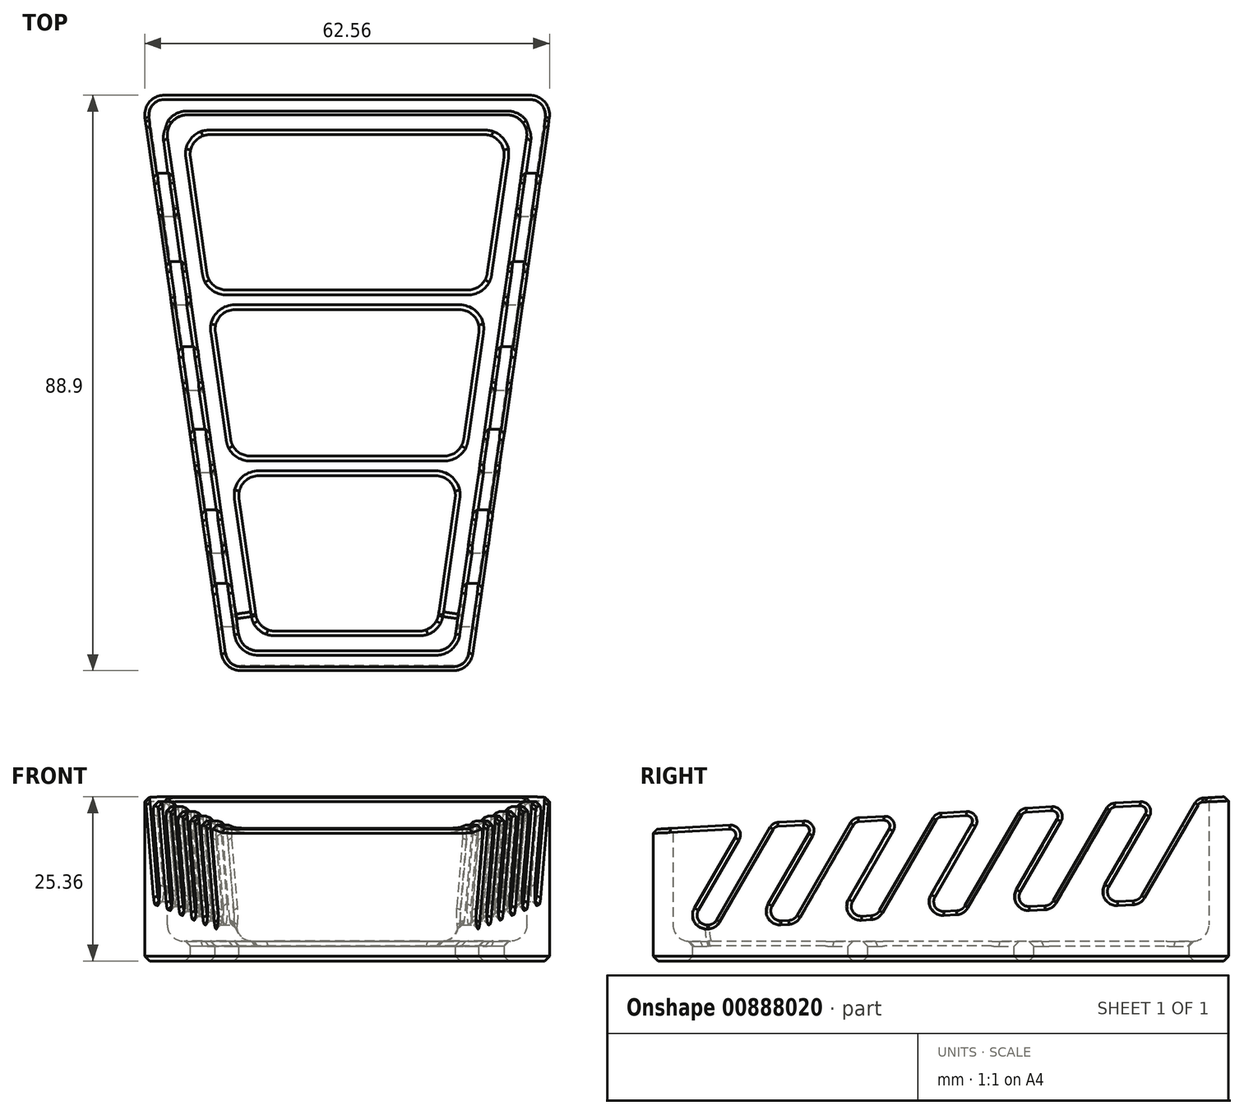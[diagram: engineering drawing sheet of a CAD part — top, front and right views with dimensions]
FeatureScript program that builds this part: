
annotation { "Feature Type Name" : "Feature", "Feature Type Description" : "" }
export const myFeature = defineFeature(function(context is Context, id is Id, definition is map)
    precondition{}
    {
        {
            var Q0;
            Q0=qCreatedBy(makeId("Top.planeOp"),FACE);
            var sketch = newSketch(context, id + "F0", { "sketchPlane" : qUnion([Q0])});
            skLineSegment(sketch, "E0", {"start": v(-122.84, 0) * mm, "end": v(0, 0) * mm, "construction": true});
            skLineSegment(sketch, "E1", {"start": v(0, 0) * mm, "end": v(0, 214.45) * mm, "construction": true});
            skLineSegment(sketch, "E2", {"start": v(-19.05, 0) * mm, "end": v(-31.75, 88.9) * mm});
            skLineSegment(sketch, "E3", {"start": v(-31.75, 88.9) * mm, "end": v(31.75, 88.9) * mm});
            skLineSegment(sketch, "E4", {"start": v(31.75, 88.9) * mm, "end": v(19.05, 0) * mm});
            skLineSegment(sketch, "E5", {"start": v(19.05, 0) * mm, "end": v(-19.05, 0) * mm});
            skSolve(sketch);
        }
        {
            var Q0;
            Q0=qSketchRegion(id+"F0",true);
            extrude(context, id + "F1", {"entities" : qUnion([Q0]), "depth" : 25.4 * mm, "offsetDistance" : 25.4 * mm});
        }
        {
            var Q0;
            Q0=makeQuery(id+"F1.opExtrude","CAP_FACE",FACE,{"disambiguationData":[OSD([sQuery(id+"F0.wireOp",EDGE,"E2"),sQuery(id+"F0.wireOp",EDGE,"E3"),sQuery(id+"F0.wireOp",EDGE,"E4"),sQuery(id+"F0.wireOp",EDGE,"E5")])],"isStart":false});
            shell(context, id + "F2", {"entities" : qUnion([Q0]), "thickness" : 3.05 * mm});
        }
        {
            var Q0;
            Q0=qCreatedBy(makeId("Right.planeOp"),FACE);
            var sketch = newSketch(context, id + "F3", { "sketchPlane" : qUnion([Q0])});
            skLineSegment(sketch, "E6", {"start": v(88.9, 38.83) * mm, "end": v(88.9, 0) * mm, "construction": true});
            skLineSegment(sketch, "E7", {"start": v(0, 38.83) * mm, "end": v(0, 0) * mm, "construction": true});
            skLineSegment(sketch, "E8", {"start": v(0, 5.08) * mm, "end": v(88.9, 10.16) * mm, "construction": true});
            skLineSegment(sketch, "E9", {"start": v(101.6, 38.83) * mm, "end": v(-12.7, 38.83) * mm});
            skLineSegment(sketch, "E10", {"start": v(-12.7, 38.83) * mm, "end": v(-12.7, 19.6) * mm});
            skLineSegment(sketch, "E11", {"start": v(101.6, 38.83) * mm, "end": v(101.6, 26.13) * mm});
            skLineSegment(sketch, "E12", {"start": v(-12.7, 19.6) * mm, "end": v(14.69, 21.16) * mm});
            skLineSegment(sketch, "E13", {"start": v(16.58, 21.27) * mm, "end": v(7.48, 5.5) * mm, "construction": true});
            skLineSegment(sketch, "E14", {"start": v(28.49, 21.95) * mm, "end": v(19.39, 6.19) * mm, "construction": true});
            skLineSegment(sketch, "E15", {"start": v(41.07, 22.67) * mm, "end": v(31.98, 6.9) * mm, "construction": true});
            skLineSegment(sketch, "E16", {"start": v(54.04, 23.4) * mm, "end": v(44.94, 7.65) * mm, "construction": true});
            skLineSegment(sketch, "E17", {"start": v(67.46, 24.17) * mm, "end": v(58.36, 8.41) * mm, "construction": true});
            skLineSegment(sketch, "E18", {"start": v(81.1, 24.95) * mm, "end": v(72.01, 9.2) * mm, "construction": true});
            skLineSegment(sketch, "E19", {"start": v(14.69, 21.16) * mm, "end": v(5.59, 5.4) * mm});
            skLineSegment(sketch, "E20", {"start": v(5.59, 5.4) * mm, "end": v(9.38, 5.62) * mm});
            skLineSegment(sketch, "E21", {"start": v(9.38, 5.62) * mm, "end": v(18.48, 21.38) * mm});
            skLineSegment(sketch, "E22", {"start": v(26.06, 21.8) * mm, "end": v(16.96, 6.05) * mm});
            skLineSegment(sketch, "E23", {"start": v(16.96, 6.05) * mm, "end": v(21.81, 6.33) * mm});
            skLineSegment(sketch, "E24", {"start": v(21.81, 6.33) * mm, "end": v(30.91, 22.09) * mm});
            skLineSegment(sketch, "E25", {"start": v(38.5, 22.52) * mm, "end": v(29.4, 6.76) * mm});
            skLineSegment(sketch, "E26", {"start": v(29.4, 6.76) * mm, "end": v(34.55, 7.05) * mm});
            skLineSegment(sketch, "E27", {"start": v(34.55, 7.05) * mm, "end": v(43.65, 22.81) * mm});
            skLineSegment(sketch, "E28", {"start": v(51.23, 23.25) * mm, "end": v(42.14, 7.49) * mm});
            skLineSegment(sketch, "E29", {"start": v(42.14, 7.49) * mm, "end": v(47.75, 7.8) * mm});
            skLineSegment(sketch, "E30", {"start": v(47.75, 7.8) * mm, "end": v(56.85, 23.57) * mm});
            skLineSegment(sketch, "E31", {"start": v(64.43, 24) * mm, "end": v(55.33, 8.24) * mm});
            skLineSegment(sketch, "E32", {"start": v(55.33, 8.24) * mm, "end": v(61.4, 8.59) * mm});
            skLineSegment(sketch, "E33", {"start": v(61.4, 8.59) * mm, "end": v(70.5, 24.35) * mm});
            skLineSegment(sketch, "E34", {"start": v(78.08, 24.78) * mm, "end": v(68.98, 9.02) * mm});
            skLineSegment(sketch, "E35", {"start": v(68.98, 9.02) * mm, "end": v(75.04, 9.37) * mm});
            skLineSegment(sketch, "E36", {"start": v(75.04, 9.37) * mm, "end": v(84.14, 25.13) * mm});
            skPoint(sketch, "E37", {"position": v(0, 20.32) * mm});
            skPoint(sketch, "E38", {"position": v(88.9, 25.4) * mm});
            skLineSegment(sketch, "E39.trimOffspring", {"start": v(18.48, 21.38) * mm, "end": v(26.06, 21.8) * mm});
            skLineSegment(sketch, "E40.trimOffspring", {"start": v(30.91, 22.09) * mm, "end": v(38.5, 22.52) * mm});
            skLineSegment(sketch, "E41.trimOffspring", {"start": v(43.65, 22.81) * mm, "end": v(51.23, 23.25) * mm});
            skLineSegment(sketch, "E42.trimOffspring", {"start": v(56.85, 23.57) * mm, "end": v(64.43, 24) * mm});
            skLineSegment(sketch, "E43.trimOffspring", {"start": v(70.5, 24.35) * mm, "end": v(78.08, 24.78) * mm});
            skLineSegment(sketch, "E44.trimOffspring", {"start": v(84.14, 25.13) * mm, "end": v(101.6, 26.13) * mm});
            skSolve(sketch);
        }
        {
            var Q0;
            Q0=makeQuery(id+"F3.imprint","IMPRINT",FACE,{"disambiguationData":[TD([[makeQuery(id+"F3.imprint","IMPRINT",EDGE,{"derivedFrom":sQuery(id+"F3.wireOp",EDGE,"E9")}),1.0]])]});
            extrude(context, id + "F4", {"entities" : qUnion([Q0]), "operationType" : NewBodyOperationType.REMOVE, "endBound" : BoundingType.THROUGH_ALL, "depth" : 25.4 * mm, "offsetDistance" : 25.4 * mm, "hasSecondDirection" : true, "secondDirectionBound" : SecondDirectionBoundingType.THROUGH_ALL, "secondDirectionOppositeDirection" : true, "secondDirectionDepth" : 25.4 * mm});
        }
        {
            var Q0;
            Q0=makeQuery(id+"F2.opShell","OFFSET_FACE",FACE,{"disambiguationData":[OSD([sQuery(id+"F0.wireOp",EDGE,"E2"),sQuery(id+"F0.wireOp",EDGE,"E3"),sQuery(id+"F0.wireOp",EDGE,"E4"),sQuery(id+"F0.wireOp",EDGE,"E5")])]});
            var sketch = newSketch(context, id + "F5", { "sketchPlane" : qUnion([Q0])});
            skLineSegment(sketch, "E45", {"start": v(-38.97, 0) * mm, "end": v(0, 0) * mm, "construction": true});
            skLineSegment(sketch, "E46", {"start": v(0, 0) * mm, "end": v(0, 92.83) * mm, "construction": true});
            skLineSegment(sketch, "E47", {"start": v(-13.76, 6.1) * mm, "end": v(13.76, 6.1) * mm});
            skLineSegment(sketch, "E48", {"start": v(13.76, 6.1) * mm, "end": v(17.2, 30.1) * mm});
            skLineSegment(sketch, "E49", {"start": v(24.72, 82.8) * mm, "end": v(-24.72, 82.8) * mm});
            skLineSegment(sketch, "E50", {"start": v(-24.72, 82.8) * mm, "end": v(-21.3, 58.8) * mm});
            skLineSegment(sketch, "E51", {"start": v(-36.35, 31.62) * mm, "end": v(27.15, 31.62) * mm, "construction": true});
            skLineSegment(sketch, "E52", {"start": v(-39.3, 57.28) * mm, "end": v(34.58, 57.28) * mm, "construction": true});
            skLineSegment(sketch, "E53", {"start": v(-17.2, 30.1) * mm, "end": v(17.2, 30.1) * mm});
            skLineSegment(sketch, "E54", {"start": v(-17.63, 33.15) * mm, "end": v(17.63, 33.15) * mm});
            skLineSegment(sketch, "E55", {"start": v(-20.86, 55.75) * mm, "end": v(20.86, 55.75) * mm});
            skLineSegment(sketch, "E56", {"start": v(-21.3, 58.8) * mm, "end": v(21.3, 58.8) * mm});
            skLineSegment(sketch, "E57.trimOffspring", {"start": v(-17.2, 30.1) * mm, "end": v(-13.76, 6.1) * mm});
            skLineSegment(sketch, "E58.trimOffspring", {"start": v(-20.86, 55.75) * mm, "end": v(-17.63, 33.15) * mm});
            skLineSegment(sketch, "E59.trimOffspring", {"start": v(21.3, 58.8) * mm, "end": v(24.72, 82.8) * mm});
            skLineSegment(sketch, "E60.trimOffspring", {"start": v(17.63, 33.15) * mm, "end": v(20.86, 55.75) * mm});
            skSolve(sketch);
        }
        {
            var Q0;
            Q0=makeQuery(id+"F5.imprint","IMPRINT",FACE,{"disambiguationData":[TD([[makeQuery(id+"F5.imprint","IMPRINT",EDGE,{"derivedFrom":sQuery(id+"F5.wireOp",EDGE,"E47")}),1.0]])]});
            var Q1;
            Q1=makeQuery(id+"F5.imprint","IMPRINT",FACE,{"disambiguationData":[TD([[makeQuery(id+"F5.imprint","IMPRINT",EDGE,{"derivedFrom":sQuery(id+"F5.wireOp",EDGE,"E54")}),1.0]])]});
            var Q2;
            Q2=makeQuery(id+"F5.imprint","IMPRINT",FACE,{"disambiguationData":[TD([[makeQuery(id+"F5.imprint","IMPRINT",EDGE,{"derivedFrom":sQuery(id+"F5.wireOp",EDGE,"E49")}),1.0]])]});
            extrude(context, id + "F6", {"entities" : qUnion([Q0, Q1, Q2]), "operationType" : NewBodyOperationType.REMOVE, "oppositeDirection" : true, "depth" : 25.4 * mm, "offsetDistance" : 25.4 * mm});
        }
        {
            var Q0;
            Q0=makeQuery(id+"F6.boolean.opBoolean","COPY",EDGE,{"derivedFrom":makeQuery(id+"F6.opExtrude","SWEPT_EDGE",EDGE,{"disambiguationData":[OSD([sQuery(id+"F5.wireOp",EDGE,"E53"),sQuery(id+"F5.wireOp",EDGE,"E57.trimOffspring")])]})});
            var Q1;
            Q1=makeQuery(id+"F6.boolean.opBoolean","COPY",EDGE,{"derivedFrom":makeQuery(id+"F6.opExtrude","SWEPT_EDGE",EDGE,{"disambiguationData":[OSD([sQuery(id+"F5.wireOp",EDGE,"E54"),sQuery(id+"F5.wireOp",EDGE,"E58.trimOffspring")])]})});
            var Q2;
            Q2=makeQuery(id+"F6.boolean.opBoolean","COPY",EDGE,{"derivedFrom":makeQuery(id+"F6.opExtrude","SWEPT_EDGE",EDGE,{"disambiguationData":[OSD([sQuery(id+"F5.wireOp",EDGE,"E55"),sQuery(id+"F5.wireOp",EDGE,"E58.trimOffspring")])]})});
            var Q3;
            Q3=makeQuery(id+"F6.boolean.opBoolean","COPY",EDGE,{"derivedFrom":makeQuery(id+"F6.opExtrude","SWEPT_EDGE",EDGE,{"disambiguationData":[OSD([sQuery(id+"F5.wireOp",EDGE,"E50"),sQuery(id+"F5.wireOp",EDGE,"E56")])]})});
            var Q4;
            Q4=makeQuery(id+"F6.boolean.opBoolean","COPY",EDGE,{"derivedFrom":makeQuery(id+"F6.opExtrude","SWEPT_EDGE",EDGE,{"disambiguationData":[OSD([sQuery(id+"F5.wireOp",EDGE,"E47"),sQuery(id+"F5.wireOp",EDGE,"E57.trimOffspring")])]})});
            var Q5;
            Q5=makeQuery(id+"F6.boolean.opBoolean","COPY",EDGE,{"derivedFrom":makeQuery(id+"F6.opExtrude","SWEPT_EDGE",EDGE,{"disambiguationData":[OSD([sQuery(id+"F5.wireOp",EDGE,"E49"),sQuery(id+"F5.wireOp",EDGE,"E50")])]})});
            var Q6;
            Q6=makeQuery(id+"F6.boolean.opBoolean","COPY",EDGE,{"derivedFrom":makeQuery(id+"F6.opExtrude","SWEPT_EDGE",EDGE,{"disambiguationData":[OSD([sQuery(id+"F5.wireOp",EDGE,"E49"),sQuery(id+"F5.wireOp",EDGE,"E59.trimOffspring")])]})});
            var Q7;
            Q7=makeQuery(id+"F6.boolean.opBoolean","COPY",EDGE,{"derivedFrom":makeQuery(id+"F6.opExtrude","SWEPT_EDGE",EDGE,{"disambiguationData":[OSD([sQuery(id+"F5.wireOp",EDGE,"E55"),sQuery(id+"F5.wireOp",EDGE,"E60.trimOffspring")])]})});
            var Q8;
            Q8=makeQuery(id+"F6.boolean.opBoolean","COPY",EDGE,{"derivedFrom":makeQuery(id+"F6.opExtrude","SWEPT_EDGE",EDGE,{"disambiguationData":[OSD([sQuery(id+"F5.wireOp",EDGE,"E48"),sQuery(id+"F5.wireOp",EDGE,"E53")])]})});
            var Q9;
            Q9=makeQuery(id+"F6.boolean.opBoolean","COPY",EDGE,{"derivedFrom":makeQuery(id+"F6.opExtrude","SWEPT_EDGE",EDGE,{"disambiguationData":[OSD([sQuery(id+"F5.wireOp",EDGE,"E47"),sQuery(id+"F5.wireOp",EDGE,"E48")])]})});
            var Q10;
            Q10=makeQuery(id+"F6.boolean.opBoolean","COPY",EDGE,{"derivedFrom":makeQuery(id+"F6.opExtrude","SWEPT_EDGE",EDGE,{"disambiguationData":[OSD([sQuery(id+"F5.wireOp",EDGE,"E54"),sQuery(id+"F5.wireOp",EDGE,"E60.trimOffspring")])]})});
            var Q11;
            Q11=makeQuery(id+"F6.boolean.opBoolean","COPY",EDGE,{"derivedFrom":makeQuery(id+"F6.opExtrude","SWEPT_EDGE",EDGE,{"disambiguationData":[OSD([sQuery(id+"F5.wireOp",EDGE,"E56"),sQuery(id+"F5.wireOp",EDGE,"E59.trimOffspring")])]})});
            fillet(context, id + "F7", {"entities" : qUnion([Q0, Q1, Q2, Q3, Q4, Q5, Q6, Q7, Q8, Q9, Q10, Q11]), "radius" : 3.05 * mm, "tangentPropagation" : true, "allowEdgeOverflow" : false});
        }
        {
            var Q0;
            {var subQ0=sQuery(id+"F0.wireOp",EDGE,"E4");var subQ1=sQuery(id+"F3.wireOp",EDGE,"E19");var subQ2=sQuery(id+"F3.wireOp",EDGE,"E20");Q0=makeQuery(id+"F4.boolean.opBoolean","COPY",EDGE,{"disambiguationData":[TD([makeQuery(id+"F1.opExtrude","SWEPT_FACE",FACE,{"disambiguationData":[OSD([subQ0])]})])],"derivedFrom":makeQuery(id+"F4.opExtrude","SWEPT_EDGE",EDGE,{"disambiguationData":[OSD([subQ1,subQ2])]})});}
            var Q1;
            {var subQ0=sQuery(id+"F0.wireOp",EDGE,"E4");var subQ1=sQuery(id+"F3.wireOp",EDGE,"E20");var subQ2=sQuery(id+"F3.wireOp",EDGE,"E21");Q1=makeQuery(id+"F4.boolean.opBoolean","COPY",EDGE,{"disambiguationData":[TD([makeQuery(id+"F1.opExtrude","SWEPT_FACE",FACE,{"disambiguationData":[OSD([subQ0])]})])],"derivedFrom":makeQuery(id+"F4.opExtrude","SWEPT_EDGE",EDGE,{"disambiguationData":[OSD([subQ1,subQ2])]})});}
            var Q2;
            {var subQ0=sQuery(id+"F0.wireOp",EDGE,"E4");var subQ1=sQuery(id+"F3.wireOp",EDGE,"E12");var subQ2=sQuery(id+"F3.wireOp",EDGE,"E19");Q2=makeQuery(id+"F4.boolean.opBoolean","COPY",EDGE,{"disambiguationData":[TD([makeQuery(id+"F1.opExtrude","SWEPT_FACE",FACE,{"disambiguationData":[OSD([subQ0])]})])],"derivedFrom":makeQuery(id+"F4.opExtrude","SWEPT_EDGE",EDGE,{"disambiguationData":[OSD([subQ1,subQ2])]})});}
            var Q3;
            {var subQ0=sQuery(id+"F0.wireOp",EDGE,"E4");var subQ1=sQuery(id+"F3.wireOp",EDGE,"E21");var subQ2=sQuery(id+"F3.wireOp",EDGE,"E39.trimOffspring");Q3=makeQuery(id+"F4.boolean.opBoolean","COPY",EDGE,{"disambiguationData":[TD([makeQuery(id+"F1.opExtrude","SWEPT_FACE",FACE,{"disambiguationData":[OSD([subQ0])]})])],"derivedFrom":makeQuery(id+"F4.opExtrude","SWEPT_EDGE",EDGE,{"disambiguationData":[OSD([subQ1,subQ2])]})});}
            var Q4;
            {var subQ0=sQuery(id+"F0.wireOp",EDGE,"E4");var subQ1=sQuery(id+"F3.wireOp",EDGE,"E22");var subQ2=sQuery(id+"F3.wireOp",EDGE,"E39.trimOffspring");Q4=makeQuery(id+"F4.boolean.opBoolean","COPY",EDGE,{"disambiguationData":[TD([makeQuery(id+"F1.opExtrude","SWEPT_FACE",FACE,{"disambiguationData":[OSD([subQ0])]})])],"derivedFrom":makeQuery(id+"F4.opExtrude","SWEPT_EDGE",EDGE,{"disambiguationData":[OSD([subQ1,subQ2])]})});}
            var Q5;
            {var subQ0=sQuery(id+"F0.wireOp",EDGE,"E4");var subQ1=sQuery(id+"F3.wireOp",EDGE,"E40.trimOffspring");var subQ2=sQuery(id+"F3.wireOp",EDGE,"E24");Q5=makeQuery(id+"F4.boolean.opBoolean","COPY",EDGE,{"disambiguationData":[TD([makeQuery(id+"F1.opExtrude","SWEPT_FACE",FACE,{"disambiguationData":[OSD([subQ0])]})])],"derivedFrom":makeQuery(id+"F4.opExtrude","SWEPT_EDGE",EDGE,{"disambiguationData":[OSD([subQ2,subQ1])]})});}
            var Q6;
            {var subQ0=sQuery(id+"F0.wireOp",EDGE,"E4");var subQ1=sQuery(id+"F3.wireOp",EDGE,"E23");var subQ2=sQuery(id+"F3.wireOp",EDGE,"E22");Q6=makeQuery(id+"F4.boolean.opBoolean","COPY",EDGE,{"disambiguationData":[TD([makeQuery(id+"F1.opExtrude","SWEPT_FACE",FACE,{"disambiguationData":[OSD([subQ0])]})])],"derivedFrom":makeQuery(id+"F4.opExtrude","SWEPT_EDGE",EDGE,{"disambiguationData":[OSD([subQ2,subQ1])]})});}
            var Q7;
            {var subQ0=sQuery(id+"F0.wireOp",EDGE,"E4");var subQ1=sQuery(id+"F3.wireOp",EDGE,"E23");var subQ2=sQuery(id+"F3.wireOp",EDGE,"E24");Q7=makeQuery(id+"F4.boolean.opBoolean","COPY",EDGE,{"disambiguationData":[TD([makeQuery(id+"F1.opExtrude","SWEPT_FACE",FACE,{"disambiguationData":[OSD([subQ0])]})])],"derivedFrom":makeQuery(id+"F4.opExtrude","SWEPT_EDGE",EDGE,{"disambiguationData":[OSD([subQ1,subQ2])]})});}
            var Q8;
            {var subQ0=sQuery(id+"F0.wireOp",EDGE,"E4");var subQ1=sQuery(id+"F3.wireOp",EDGE,"E40.trimOffspring");var subQ2=sQuery(id+"F3.wireOp",EDGE,"E25");Q8=makeQuery(id+"F4.boolean.opBoolean","COPY",EDGE,{"disambiguationData":[TD([makeQuery(id+"F1.opExtrude","SWEPT_FACE",FACE,{"disambiguationData":[OSD([subQ0])]})])],"derivedFrom":makeQuery(id+"F4.opExtrude","SWEPT_EDGE",EDGE,{"disambiguationData":[OSD([subQ2,subQ1])]})});}
            var Q9;
            {var subQ0=sQuery(id+"F0.wireOp",EDGE,"E4");var subQ1=sQuery(id+"F3.wireOp",EDGE,"E27");var subQ2=sQuery(id+"F3.wireOp",EDGE,"E41.trimOffspring");Q9=makeQuery(id+"F4.boolean.opBoolean","COPY",EDGE,{"disambiguationData":[TD([makeQuery(id+"F1.opExtrude","SWEPT_FACE",FACE,{"disambiguationData":[OSD([subQ0])]})])],"derivedFrom":makeQuery(id+"F4.opExtrude","SWEPT_EDGE",EDGE,{"disambiguationData":[OSD([subQ1,subQ2])]})});}
            var Q10;
            {var subQ0=sQuery(id+"F0.wireOp",EDGE,"E4");var subQ1=sQuery(id+"F3.wireOp",EDGE,"E26");var subQ2=sQuery(id+"F3.wireOp",EDGE,"E27");Q10=makeQuery(id+"F4.boolean.opBoolean","COPY",EDGE,{"disambiguationData":[TD([makeQuery(id+"F1.opExtrude","SWEPT_FACE",FACE,{"disambiguationData":[OSD([subQ0])]})])],"derivedFrom":makeQuery(id+"F4.opExtrude","SWEPT_EDGE",EDGE,{"disambiguationData":[OSD([subQ1,subQ2])]})});}
            var Q11;
            {var subQ0=sQuery(id+"F0.wireOp",EDGE,"E4");var subQ1=sQuery(id+"F3.wireOp",EDGE,"E25");var subQ2=sQuery(id+"F3.wireOp",EDGE,"E26");Q11=makeQuery(id+"F4.boolean.opBoolean","COPY",EDGE,{"disambiguationData":[TD([makeQuery(id+"F1.opExtrude","SWEPT_FACE",FACE,{"disambiguationData":[OSD([subQ0])]})])],"derivedFrom":makeQuery(id+"F4.opExtrude","SWEPT_EDGE",EDGE,{"disambiguationData":[OSD([subQ1,subQ2])]})});}
            var Q12;
            {var subQ0=sQuery(id+"F0.wireOp",EDGE,"E4");var subQ1=sQuery(id+"F3.wireOp",EDGE,"E28");var subQ2=sQuery(id+"F3.wireOp",EDGE,"E29");Q12=makeQuery(id+"F4.boolean.opBoolean","COPY",EDGE,{"disambiguationData":[TD([makeQuery(id+"F1.opExtrude","SWEPT_FACE",FACE,{"disambiguationData":[OSD([subQ0])]})])],"derivedFrom":makeQuery(id+"F4.opExtrude","SWEPT_EDGE",EDGE,{"disambiguationData":[OSD([subQ1,subQ2])]})});}
            var Q13;
            {var subQ0=sQuery(id+"F0.wireOp",EDGE,"E4");var subQ1=sQuery(id+"F3.wireOp",EDGE,"E28");var subQ2=sQuery(id+"F3.wireOp",EDGE,"E41.trimOffspring");Q13=makeQuery(id+"F4.boolean.opBoolean","COPY",EDGE,{"disambiguationData":[TD([makeQuery(id+"F1.opExtrude","SWEPT_FACE",FACE,{"disambiguationData":[OSD([subQ0])]})])],"derivedFrom":makeQuery(id+"F4.opExtrude","SWEPT_EDGE",EDGE,{"disambiguationData":[OSD([subQ1,subQ2])]})});}
            var Q14;
            {var subQ0=sQuery(id+"F0.wireOp",EDGE,"E4");var subQ1=sQuery(id+"F3.wireOp",EDGE,"E30");var subQ2=sQuery(id+"F3.wireOp",EDGE,"E42.trimOffspring");Q14=makeQuery(id+"F4.boolean.opBoolean","COPY",EDGE,{"disambiguationData":[TD([makeQuery(id+"F1.opExtrude","SWEPT_FACE",FACE,{"disambiguationData":[OSD([subQ0])]})])],"derivedFrom":makeQuery(id+"F4.opExtrude","SWEPT_EDGE",EDGE,{"disambiguationData":[OSD([subQ1,subQ2])]})});}
            var Q15;
            {var subQ0=sQuery(id+"F0.wireOp",EDGE,"E4");var subQ1=sQuery(id+"F3.wireOp",EDGE,"E29");var subQ2=sQuery(id+"F3.wireOp",EDGE,"E30");Q15=makeQuery(id+"F4.boolean.opBoolean","COPY",EDGE,{"disambiguationData":[TD([makeQuery(id+"F1.opExtrude","SWEPT_FACE",FACE,{"disambiguationData":[OSD([subQ0])]})])],"derivedFrom":makeQuery(id+"F4.opExtrude","SWEPT_EDGE",EDGE,{"disambiguationData":[OSD([subQ1,subQ2])]})});}
            var Q16;
            {var subQ0=sQuery(id+"F0.wireOp",EDGE,"E4");var subQ1=sQuery(id+"F3.wireOp",EDGE,"E33");var subQ2=sQuery(id+"F3.wireOp",EDGE,"E43.trimOffspring");Q16=makeQuery(id+"F4.boolean.opBoolean","COPY",EDGE,{"disambiguationData":[TD([makeQuery(id+"F1.opExtrude","SWEPT_FACE",FACE,{"disambiguationData":[OSD([subQ0])]})])],"derivedFrom":makeQuery(id+"F4.opExtrude","SWEPT_EDGE",EDGE,{"disambiguationData":[OSD([subQ1,subQ2])]})});}
            var Q17;
            {var subQ0=sQuery(id+"F0.wireOp",EDGE,"E4");var subQ1=sQuery(id+"F3.wireOp",EDGE,"E31");var subQ2=sQuery(id+"F3.wireOp",EDGE,"E42.trimOffspring");Q17=makeQuery(id+"F4.boolean.opBoolean","COPY",EDGE,{"disambiguationData":[TD([makeQuery(id+"F1.opExtrude","SWEPT_FACE",FACE,{"disambiguationData":[OSD([subQ0])]})])],"derivedFrom":makeQuery(id+"F4.opExtrude","SWEPT_EDGE",EDGE,{"disambiguationData":[OSD([subQ1,subQ2])]})});}
            var Q18;
            {var subQ0=sQuery(id+"F0.wireOp",EDGE,"E4");var subQ1=sQuery(id+"F3.wireOp",EDGE,"E33");var subQ2=sQuery(id+"F3.wireOp",EDGE,"E32");Q18=makeQuery(id+"F4.boolean.opBoolean","COPY",EDGE,{"disambiguationData":[TD([makeQuery(id+"F1.opExtrude","SWEPT_FACE",FACE,{"disambiguationData":[OSD([subQ0])]})])],"derivedFrom":makeQuery(id+"F4.opExtrude","SWEPT_EDGE",EDGE,{"disambiguationData":[OSD([subQ2,subQ1])]})});}
            var Q19;
            {var subQ0=sQuery(id+"F0.wireOp",EDGE,"E4");var subQ1=sQuery(id+"F3.wireOp",EDGE,"E31");var subQ2=sQuery(id+"F3.wireOp",EDGE,"E32");Q19=makeQuery(id+"F4.boolean.opBoolean","COPY",EDGE,{"disambiguationData":[TD([makeQuery(id+"F1.opExtrude","SWEPT_FACE",FACE,{"disambiguationData":[OSD([subQ0])]})])],"derivedFrom":makeQuery(id+"F4.opExtrude","SWEPT_EDGE",EDGE,{"disambiguationData":[OSD([subQ1,subQ2])]})});}
            var Q20;
            {var subQ0=sQuery(id+"F0.wireOp",EDGE,"E4");var subQ1=sQuery(id+"F3.wireOp",EDGE,"E34");var subQ2=sQuery(id+"F3.wireOp",EDGE,"E43.trimOffspring");Q20=makeQuery(id+"F4.boolean.opBoolean","COPY",EDGE,{"disambiguationData":[TD([makeQuery(id+"F1.opExtrude","SWEPT_FACE",FACE,{"disambiguationData":[OSD([subQ0])]})])],"derivedFrom":makeQuery(id+"F4.opExtrude","SWEPT_EDGE",EDGE,{"disambiguationData":[OSD([subQ1,subQ2])]})});}
            var Q21;
            {var subQ0=sQuery(id+"F0.wireOp",EDGE,"E4");var subQ1=sQuery(id+"F3.wireOp",EDGE,"E35");var subQ2=sQuery(id+"F3.wireOp",EDGE,"E36");Q21=makeQuery(id+"F4.boolean.opBoolean","COPY",EDGE,{"disambiguationData":[TD([makeQuery(id+"F1.opExtrude","SWEPT_FACE",FACE,{"disambiguationData":[OSD([subQ0])]})])],"derivedFrom":makeQuery(id+"F4.opExtrude","SWEPT_EDGE",EDGE,{"disambiguationData":[OSD([subQ1,subQ2])]})});}
            var Q22;
            {var subQ0=sQuery(id+"F0.wireOp",EDGE,"E4");var subQ1=sQuery(id+"F3.wireOp",EDGE,"E34");var subQ2=sQuery(id+"F3.wireOp",EDGE,"E35");Q22=makeQuery(id+"F4.boolean.opBoolean","COPY",EDGE,{"disambiguationData":[TD([makeQuery(id+"F1.opExtrude","SWEPT_FACE",FACE,{"disambiguationData":[OSD([subQ0])]})])],"derivedFrom":makeQuery(id+"F4.opExtrude","SWEPT_EDGE",EDGE,{"disambiguationData":[OSD([subQ1,subQ2])]})});}
            var Q23;
            Q23=makeQuery(id+"F4.boolean.opBoolean","COPY",EDGE,{"derivedFrom":makeQuery(id+"F4.opExtrude","SWEPT_EDGE",EDGE,{"disambiguationData":[OSD([sQuery(id+"F3.wireOp",EDGE,"E36"),sQuery(id+"F3.wireOp",EDGE,"E44.trimOffspring")])]})});
            var Q24;
            {var subQ0=sQuery(id+"F0.wireOp",EDGE,"E2");var subQ1=sQuery(id+"F3.wireOp",EDGE,"E19");var subQ2=sQuery(id+"F3.wireOp",EDGE,"E12");Q24=makeQuery(id+"F4.boolean.opBoolean","COPY",EDGE,{"disambiguationData":[TD([makeQuery(id+"F1.opExtrude","SWEPT_FACE",FACE,{"disambiguationData":[OSD([subQ0])]})])],"derivedFrom":makeQuery(id+"F4.opExtrude","SWEPT_EDGE",EDGE,{"disambiguationData":[OSD([subQ2,subQ1])]})});}
            var Q25;
            {var subQ0=sQuery(id+"F0.wireOp",EDGE,"E2");var subQ1=sQuery(id+"F3.wireOp",EDGE,"E19");var subQ2=sQuery(id+"F3.wireOp",EDGE,"E20");Q25=makeQuery(id+"F4.boolean.opBoolean","COPY",EDGE,{"disambiguationData":[TD([makeQuery(id+"F1.opExtrude","SWEPT_FACE",FACE,{"disambiguationData":[OSD([subQ0])]})])],"derivedFrom":makeQuery(id+"F4.opExtrude","SWEPT_EDGE",EDGE,{"disambiguationData":[OSD([subQ1,subQ2])]})});}
            var Q26;
            {var subQ0=sQuery(id+"F0.wireOp",EDGE,"E2");var subQ1=sQuery(id+"F3.wireOp",EDGE,"E21");var subQ2=sQuery(id+"F3.wireOp",EDGE,"E39.trimOffspring");Q26=makeQuery(id+"F4.boolean.opBoolean","COPY",EDGE,{"disambiguationData":[TD([makeQuery(id+"F1.opExtrude","SWEPT_FACE",FACE,{"disambiguationData":[OSD([subQ0])]})])],"derivedFrom":makeQuery(id+"F4.opExtrude","SWEPT_EDGE",EDGE,{"disambiguationData":[OSD([subQ1,subQ2])]})});}
            var Q27;
            {var subQ0=sQuery(id+"F0.wireOp",EDGE,"E2");var subQ1=sQuery(id+"F3.wireOp",EDGE,"E22");var subQ2=sQuery(id+"F3.wireOp",EDGE,"E39.trimOffspring");Q27=makeQuery(id+"F4.boolean.opBoolean","COPY",EDGE,{"disambiguationData":[TD([makeQuery(id+"F1.opExtrude","SWEPT_FACE",FACE,{"disambiguationData":[OSD([subQ0])]})])],"derivedFrom":makeQuery(id+"F4.opExtrude","SWEPT_EDGE",EDGE,{"disambiguationData":[OSD([subQ1,subQ2])]})});}
            var Q28;
            {var subQ0=sQuery(id+"F0.wireOp",EDGE,"E2");var subQ1=sQuery(id+"F3.wireOp",EDGE,"E22");var subQ2=sQuery(id+"F3.wireOp",EDGE,"E23");Q28=makeQuery(id+"F4.boolean.opBoolean","COPY",EDGE,{"disambiguationData":[TD([makeQuery(id+"F1.opExtrude","SWEPT_FACE",FACE,{"disambiguationData":[OSD([subQ0])]})])],"derivedFrom":makeQuery(id+"F4.opExtrude","SWEPT_EDGE",EDGE,{"disambiguationData":[OSD([subQ1,subQ2])]})});}
            var Q29;
            {var subQ0=sQuery(id+"F0.wireOp",EDGE,"E2");var subQ1=sQuery(id+"F3.wireOp",EDGE,"E20");var subQ2=sQuery(id+"F3.wireOp",EDGE,"E21");Q29=makeQuery(id+"F4.boolean.opBoolean","COPY",EDGE,{"disambiguationData":[TD([makeQuery(id+"F1.opExtrude","SWEPT_FACE",FACE,{"disambiguationData":[OSD([subQ0])]})])],"derivedFrom":makeQuery(id+"F4.opExtrude","SWEPT_EDGE",EDGE,{"disambiguationData":[OSD([subQ1,subQ2])]})});}
            var Q30;
            {var subQ0=sQuery(id+"F0.wireOp",EDGE,"E2");var subQ1=sQuery(id+"F3.wireOp",EDGE,"E24");var subQ2=sQuery(id+"F3.wireOp",EDGE,"E23");Q30=makeQuery(id+"F4.boolean.opBoolean","COPY",EDGE,{"disambiguationData":[TD([makeQuery(id+"F1.opExtrude","SWEPT_FACE",FACE,{"disambiguationData":[OSD([subQ0])]})])],"derivedFrom":makeQuery(id+"F4.opExtrude","SWEPT_EDGE",EDGE,{"disambiguationData":[OSD([subQ2,subQ1])]})});}
            var Q31;
            {var subQ0=sQuery(id+"F0.wireOp",EDGE,"E2");var subQ1=sQuery(id+"F3.wireOp",EDGE,"E24");var subQ2=sQuery(id+"F3.wireOp",EDGE,"E40.trimOffspring");Q31=makeQuery(id+"F4.boolean.opBoolean","COPY",EDGE,{"disambiguationData":[TD([makeQuery(id+"F1.opExtrude","SWEPT_FACE",FACE,{"disambiguationData":[OSD([subQ0])]})])],"derivedFrom":makeQuery(id+"F4.opExtrude","SWEPT_EDGE",EDGE,{"disambiguationData":[OSD([subQ1,subQ2])]})});}
            var Q32;
            {var subQ0=sQuery(id+"F0.wireOp",EDGE,"E2");var subQ1=sQuery(id+"F3.wireOp",EDGE,"E41.trimOffspring");var subQ2=sQuery(id+"F3.wireOp",EDGE,"E27");Q32=makeQuery(id+"F4.boolean.opBoolean","COPY",EDGE,{"disambiguationData":[TD([makeQuery(id+"F1.opExtrude","SWEPT_FACE",FACE,{"disambiguationData":[OSD([subQ0])]})])],"derivedFrom":makeQuery(id+"F4.opExtrude","SWEPT_EDGE",EDGE,{"disambiguationData":[OSD([subQ2,subQ1])]})});}
            var Q33;
            {var subQ0=sQuery(id+"F0.wireOp",EDGE,"E2");var subQ1=sQuery(id+"F3.wireOp",EDGE,"E26");var subQ2=sQuery(id+"F3.wireOp",EDGE,"E27");Q33=makeQuery(id+"F4.boolean.opBoolean","COPY",EDGE,{"disambiguationData":[TD([makeQuery(id+"F1.opExtrude","SWEPT_FACE",FACE,{"disambiguationData":[OSD([subQ0])]})])],"derivedFrom":makeQuery(id+"F4.opExtrude","SWEPT_EDGE",EDGE,{"disambiguationData":[OSD([subQ1,subQ2])]})});}
            var Q34;
            {var subQ0=sQuery(id+"F0.wireOp",EDGE,"E2");var subQ1=sQuery(id+"F3.wireOp",EDGE,"E25");var subQ2=sQuery(id+"F3.wireOp",EDGE,"E40.trimOffspring");Q34=makeQuery(id+"F4.boolean.opBoolean","COPY",EDGE,{"disambiguationData":[TD([makeQuery(id+"F1.opExtrude","SWEPT_FACE",FACE,{"disambiguationData":[OSD([subQ0])]})])],"derivedFrom":makeQuery(id+"F4.opExtrude","SWEPT_EDGE",EDGE,{"disambiguationData":[OSD([subQ1,subQ2])]})});}
            var Q35;
            {var subQ0=sQuery(id+"F0.wireOp",EDGE,"E2");var subQ1=sQuery(id+"F3.wireOp",EDGE,"E25");var subQ2=sQuery(id+"F3.wireOp",EDGE,"E26");Q35=makeQuery(id+"F4.boolean.opBoolean","COPY",EDGE,{"disambiguationData":[TD([makeQuery(id+"F1.opExtrude","SWEPT_FACE",FACE,{"disambiguationData":[OSD([subQ0])]})])],"derivedFrom":makeQuery(id+"F4.opExtrude","SWEPT_EDGE",EDGE,{"disambiguationData":[OSD([subQ1,subQ2])]})});}
            var Q36;
            {var subQ0=sQuery(id+"F0.wireOp",EDGE,"E2");var subQ1=sQuery(id+"F3.wireOp",EDGE,"E29");var subQ2=sQuery(id+"F3.wireOp",EDGE,"E28");Q36=makeQuery(id+"F4.boolean.opBoolean","COPY",EDGE,{"disambiguationData":[TD([makeQuery(id+"F1.opExtrude","SWEPT_FACE",FACE,{"disambiguationData":[OSD([subQ0])]})])],"derivedFrom":makeQuery(id+"F4.opExtrude","SWEPT_EDGE",EDGE,{"disambiguationData":[OSD([subQ2,subQ1])]})});}
            var Q37;
            {var subQ0=sQuery(id+"F0.wireOp",EDGE,"E2");var subQ1=sQuery(id+"F3.wireOp",EDGE,"E41.trimOffspring");var subQ2=sQuery(id+"F3.wireOp",EDGE,"E28");Q37=makeQuery(id+"F4.boolean.opBoolean","COPY",EDGE,{"disambiguationData":[TD([makeQuery(id+"F1.opExtrude","SWEPT_FACE",FACE,{"disambiguationData":[OSD([subQ0])]})])],"derivedFrom":makeQuery(id+"F4.opExtrude","SWEPT_EDGE",EDGE,{"disambiguationData":[OSD([subQ2,subQ1])]})});}
            var Q38;
            {var subQ0=sQuery(id+"F0.wireOp",EDGE,"E2");var subQ1=sQuery(id+"F3.wireOp",EDGE,"E30");var subQ2=sQuery(id+"F3.wireOp",EDGE,"E42.trimOffspring");Q38=makeQuery(id+"F4.boolean.opBoolean","COPY",EDGE,{"disambiguationData":[TD([makeQuery(id+"F1.opExtrude","SWEPT_FACE",FACE,{"disambiguationData":[OSD([subQ0])]})])],"derivedFrom":makeQuery(id+"F4.opExtrude","SWEPT_EDGE",EDGE,{"disambiguationData":[OSD([subQ1,subQ2])]})});}
            var Q39;
            {var subQ0=sQuery(id+"F0.wireOp",EDGE,"E2");var subQ1=sQuery(id+"F3.wireOp",EDGE,"E31");var subQ2=sQuery(id+"F3.wireOp",EDGE,"E32");Q39=makeQuery(id+"F4.boolean.opBoolean","COPY",EDGE,{"disambiguationData":[TD([makeQuery(id+"F1.opExtrude","SWEPT_FACE",FACE,{"disambiguationData":[OSD([subQ0])]})])],"derivedFrom":makeQuery(id+"F4.opExtrude","SWEPT_EDGE",EDGE,{"disambiguationData":[OSD([subQ1,subQ2])]})});}
            var Q40;
            {var subQ0=sQuery(id+"F0.wireOp",EDGE,"E2");var subQ1=sQuery(id+"F3.wireOp",EDGE,"E33");var subQ2=sQuery(id+"F3.wireOp",EDGE,"E43.trimOffspring");Q40=makeQuery(id+"F4.boolean.opBoolean","COPY",EDGE,{"disambiguationData":[TD([makeQuery(id+"F1.opExtrude","SWEPT_FACE",FACE,{"disambiguationData":[OSD([subQ0])]})])],"derivedFrom":makeQuery(id+"F4.opExtrude","SWEPT_EDGE",EDGE,{"disambiguationData":[OSD([subQ1,subQ2])]})});}
            var Q41;
            {var subQ0=sQuery(id+"F0.wireOp",EDGE,"E2");var subQ1=sQuery(id+"F3.wireOp",EDGE,"E42.trimOffspring");var subQ2=sQuery(id+"F3.wireOp",EDGE,"E31");Q41=makeQuery(id+"F4.boolean.opBoolean","COPY",EDGE,{"disambiguationData":[TD([makeQuery(id+"F1.opExtrude","SWEPT_FACE",FACE,{"disambiguationData":[OSD([subQ0])]})])],"derivedFrom":makeQuery(id+"F4.opExtrude","SWEPT_EDGE",EDGE,{"disambiguationData":[OSD([subQ2,subQ1])]})});}
            var Q42;
            {var subQ0=sQuery(id+"F0.wireOp",EDGE,"E2");var subQ1=sQuery(id+"F3.wireOp",EDGE,"E29");var subQ2=sQuery(id+"F3.wireOp",EDGE,"E30");Q42=makeQuery(id+"F4.boolean.opBoolean","COPY",EDGE,{"disambiguationData":[TD([makeQuery(id+"F1.opExtrude","SWEPT_FACE",FACE,{"disambiguationData":[OSD([subQ0])]})])],"derivedFrom":makeQuery(id+"F4.opExtrude","SWEPT_EDGE",EDGE,{"disambiguationData":[OSD([subQ1,subQ2])]})});}
            var Q43;
            {var subQ0=sQuery(id+"F0.wireOp",EDGE,"E2");var subQ1=sQuery(id+"F3.wireOp",EDGE,"E32");var subQ2=sQuery(id+"F3.wireOp",EDGE,"E33");Q43=makeQuery(id+"F4.boolean.opBoolean","COPY",EDGE,{"disambiguationData":[TD([makeQuery(id+"F1.opExtrude","SWEPT_FACE",FACE,{"disambiguationData":[OSD([subQ0])]})])],"derivedFrom":makeQuery(id+"F4.opExtrude","SWEPT_EDGE",EDGE,{"disambiguationData":[OSD([subQ1,subQ2])]})});}
            var Q44;
            {var subQ0=sQuery(id+"F0.wireOp",EDGE,"E2");var subQ1=sQuery(id+"F3.wireOp",EDGE,"E35");var subQ2=sQuery(id+"F3.wireOp",EDGE,"E36");Q44=makeQuery(id+"F4.boolean.opBoolean","COPY",EDGE,{"disambiguationData":[TD([makeQuery(id+"F1.opExtrude","SWEPT_FACE",FACE,{"disambiguationData":[OSD([subQ0])]})])],"derivedFrom":makeQuery(id+"F4.opExtrude","SWEPT_EDGE",EDGE,{"disambiguationData":[OSD([subQ1,subQ2])]})});}
            var Q45;
            {var subQ0=sQuery(id+"F0.wireOp",EDGE,"E2");var subQ1=sQuery(id+"F3.wireOp",EDGE,"E34");var subQ2=sQuery(id+"F3.wireOp",EDGE,"E35");Q45=makeQuery(id+"F4.boolean.opBoolean","COPY",EDGE,{"disambiguationData":[TD([makeQuery(id+"F1.opExtrude","SWEPT_FACE",FACE,{"disambiguationData":[OSD([subQ0])]})])],"derivedFrom":makeQuery(id+"F4.opExtrude","SWEPT_EDGE",EDGE,{"disambiguationData":[OSD([subQ1,subQ2])]})});}
            var Q46;
            {var subQ0=sQuery(id+"F0.wireOp",EDGE,"E2");var subQ1=sQuery(id+"F3.wireOp",EDGE,"E34");var subQ2=sQuery(id+"F3.wireOp",EDGE,"E43.trimOffspring");Q46=makeQuery(id+"F4.boolean.opBoolean","COPY",EDGE,{"disambiguationData":[TD([makeQuery(id+"F1.opExtrude","SWEPT_FACE",FACE,{"disambiguationData":[OSD([subQ0])]})])],"derivedFrom":makeQuery(id+"F4.opExtrude","SWEPT_EDGE",EDGE,{"disambiguationData":[OSD([subQ1,subQ2])]})});}
            fillet(context, id + "F8", {"entities" : qUnion([Q0, Q1, Q2, Q3, Q4, Q5, Q6, Q7, Q8, Q9, Q10, Q11, Q12, Q13, Q14, Q15, Q16, Q17, Q18, Q19, Q20, Q21, Q22, Q23, Q24, Q25, Q26, Q27, Q28, Q29, Q30, Q31, Q32, Q33, Q34, Q35, Q36, Q37, Q38, Q39, Q40, Q41, Q42, Q43, Q44, Q45, Q46]), "radius" : 1.52 * mm, "tangentPropagation" : true, "allowEdgeOverflow" : false});
        }
        {
            var Q0;
            Q0=makeQuery(id+"F2.opShell","OFFSET_EDGE",EDGE,{"disambiguationData":[OSD([sQuery(id+"F0.wireOp",EDGE,"E3"),sQuery(id+"F0.wireOp",EDGE,"E4")])]});
            var Q1;
            Q1=makeQuery(id+"F2.opShell","OFFSET_EDGE",EDGE,{"disambiguationData":[OSD([sQuery(id+"F0.wireOp",EDGE,"E2"),sQuery(id+"F0.wireOp",EDGE,"E3")])]});
            var Q2;
            Q2=makeQuery(id+"F2.opShell","OFFSET_EDGE",EDGE,{"disambiguationData":[OSD([sQuery(id+"F0.wireOp",EDGE,"E2"),sQuery(id+"F0.wireOp",EDGE,"E5")])]});
            var Q3;
            Q3=makeQuery(id+"F2.opShell","OFFSET_EDGE",EDGE,{"disambiguationData":[OSD([sQuery(id+"F0.wireOp",EDGE,"E4"),sQuery(id+"F0.wireOp",EDGE,"E5")])]});
            var Q4;
            Q4=makeQuery(id+"F1.opExtrude","SWEPT_EDGE",EDGE,{"disambiguationData":[OSD([sQuery(id+"F0.wireOp",EDGE,"E4"),sQuery(id+"F0.wireOp",EDGE,"E5")])]});
            var Q5;
            Q5=makeQuery(id+"F1.opExtrude","SWEPT_EDGE",EDGE,{"disambiguationData":[OSD([sQuery(id+"F0.wireOp",EDGE,"E3"),sQuery(id+"F0.wireOp",EDGE,"E4")])]});
            var Q6;
            Q6=makeQuery(id+"F1.opExtrude","SWEPT_EDGE",EDGE,{"disambiguationData":[OSD([sQuery(id+"F0.wireOp",EDGE,"E2"),sQuery(id+"F0.wireOp",EDGE,"E3")])]});
            var Q7;
            Q7=makeQuery(id+"F1.opExtrude","SWEPT_EDGE",EDGE,{"disambiguationData":[OSD([sQuery(id+"F0.wireOp",EDGE,"E2"),sQuery(id+"F0.wireOp",EDGE,"E5")])]});
            fillet(context, id + "F9", {"entities" : qUnion([Q0, Q1, Q2, Q3, Q4, Q5, Q6, Q7]), "radius" : 3.05 * mm, "tangentPropagation" : true, "allowEdgeOverflow" : false});
        }
        {
            var Q0;
            {var subQ0=sQuery(id+"F0.wireOp",EDGE,"E4");Q0=makeQuery(id+"F2.opShell","OFFSET_EDGE",EDGE,{"disambiguationData":[OSD([subQ0]),TDD([makeQuery(id+"F1.opExtrude","CAP_EDGE",EDGE,{"disambiguationData":[OSD([subQ0])],"isStart":true})])]});}
            fillet(context, id + "F10", {"entities" : qUnion([Q0]), "radius" : 2.54 * mm, "tangentPropagation" : true, "allowEdgeOverflow" : false});
        }
        {
            var Q0;
            Q0=makeQuery(id+"F1.opExtrude","CAP_FACE",FACE,{"disambiguationData":[OSD([sQuery(id+"F0.wireOp",EDGE,"E2"),sQuery(id+"F0.wireOp",EDGE,"E3"),sQuery(id+"F0.wireOp",EDGE,"E4"),sQuery(id+"F0.wireOp",EDGE,"E5")])],"isStart":true});
            var Q1;
            Q1=makeQuery(id+"F7.opFillet","BLEND_EDGE",EDGE,{"blendedFrom":[makeQuery(id+"F6.boolean.opBoolean","COPY",EDGE,{"derivedFrom":makeQuery(id+"F6.opExtrude","SWEPT_EDGE",EDGE,{"disambiguationData":[OSD([sQuery(id+"F5.wireOp",EDGE,"E53"),sQuery(id+"F5.wireOp",EDGE,"E57.trimOffspring")])]})}),makeQuery(id+"F2.opShell","OFFSET_FACE",FACE,{"disambiguationData":[OSD([sQuery(id+"F0.wireOp",EDGE,"E2"),sQuery(id+"F0.wireOp",EDGE,"E3"),sQuery(id+"F0.wireOp",EDGE,"E4"),sQuery(id+"F0.wireOp",EDGE,"E5")])]})],"blendedInto":[makeQuery(id+"F2.opShell","OFFSET_FACE",FACE,{"disambiguationData":[OSD([sQuery(id+"F0.wireOp",EDGE,"E2"),sQuery(id+"F0.wireOp",EDGE,"E3"),sQuery(id+"F0.wireOp",EDGE,"E4"),sQuery(id+"F0.wireOp",EDGE,"E5")])]})]});
            var Q2;
            Q2=makeQuery(id+"F7.opFillet","BLEND_EDGE",EDGE,{"blendedFrom":[makeQuery(id+"F6.boolean.opBoolean","COPY",EDGE,{"derivedFrom":makeQuery(id+"F6.opExtrude","SWEPT_EDGE",EDGE,{"disambiguationData":[OSD([sQuery(id+"F5.wireOp",EDGE,"E54"),sQuery(id+"F5.wireOp",EDGE,"E58.trimOffspring")])]})}),makeQuery(id+"F2.opShell","OFFSET_FACE",FACE,{"disambiguationData":[OSD([sQuery(id+"F0.wireOp",EDGE,"E2"),sQuery(id+"F0.wireOp",EDGE,"E3"),sQuery(id+"F0.wireOp",EDGE,"E4"),sQuery(id+"F0.wireOp",EDGE,"E5")])]})],"blendedInto":[makeQuery(id+"F2.opShell","OFFSET_FACE",FACE,{"disambiguationData":[OSD([sQuery(id+"F0.wireOp",EDGE,"E2"),sQuery(id+"F0.wireOp",EDGE,"E3"),sQuery(id+"F0.wireOp",EDGE,"E4"),sQuery(id+"F0.wireOp",EDGE,"E5")])]})]});
            var Q3;
            Q3=makeQuery(id+"F7.opFillet","BLEND_EDGE",EDGE,{"blendedFrom":[makeQuery(id+"F6.boolean.opBoolean","COPY",EDGE,{"derivedFrom":makeQuery(id+"F6.opExtrude","SWEPT_EDGE",EDGE,{"disambiguationData":[OSD([sQuery(id+"F5.wireOp",EDGE,"E50"),sQuery(id+"F5.wireOp",EDGE,"E56")])]})}),makeQuery(id+"F2.opShell","OFFSET_FACE",FACE,{"disambiguationData":[OSD([sQuery(id+"F0.wireOp",EDGE,"E2"),sQuery(id+"F0.wireOp",EDGE,"E3"),sQuery(id+"F0.wireOp",EDGE,"E4"),sQuery(id+"F0.wireOp",EDGE,"E5")])]})],"blendedInto":[makeQuery(id+"F2.opShell","OFFSET_FACE",FACE,{"disambiguationData":[OSD([sQuery(id+"F0.wireOp",EDGE,"E2"),sQuery(id+"F0.wireOp",EDGE,"E3"),sQuery(id+"F0.wireOp",EDGE,"E4"),sQuery(id+"F0.wireOp",EDGE,"E5")])]})]});
            chamfer(context, id + "F11", {"entities" : qUnion([Q0, Q1, Q2, Q3]), "width" : 0.76 * mm, "tangentPropagation" : true});
        }
        {
            var Q0;
            Q0=makeQuery(id+"F4.boolean.opBoolean","INTERSECT",EDGE,{"derivedFrom":[makeQuery(id+"F1.opExtrude","SWEPT_FACE",FACE,{"disambiguationData":[OSD([sQuery(id+"F0.wireOp",EDGE,"E4")])]}),makeQuery(id+"F4.opExtrude","SWEPT_FACE",FACE,{"disambiguationData":[OSD([sQuery(id+"F3.wireOp",EDGE,"E41.trimOffspring")])]})]});
            var Q1;
            Q1=makeQuery(id+"F4.boolean.opBoolean","INTERSECT",EDGE,{"derivedFrom":[makeQuery(id+"F2.opShell","OFFSET_FACE",FACE,{"disambiguationData":[OSD([sQuery(id+"F0.wireOp",EDGE,"E4")])]}),makeQuery(id+"F4.opExtrude","SWEPT_FACE",FACE,{"disambiguationData":[OSD([sQuery(id+"F3.wireOp",EDGE,"E42.trimOffspring")])]})]});
            chamfer(context, id + "F12", {"entities" : qUnion([Q0, Q1]), "width" : 0.64 * mm, "tangentPropagation" : true});
        }
    });
